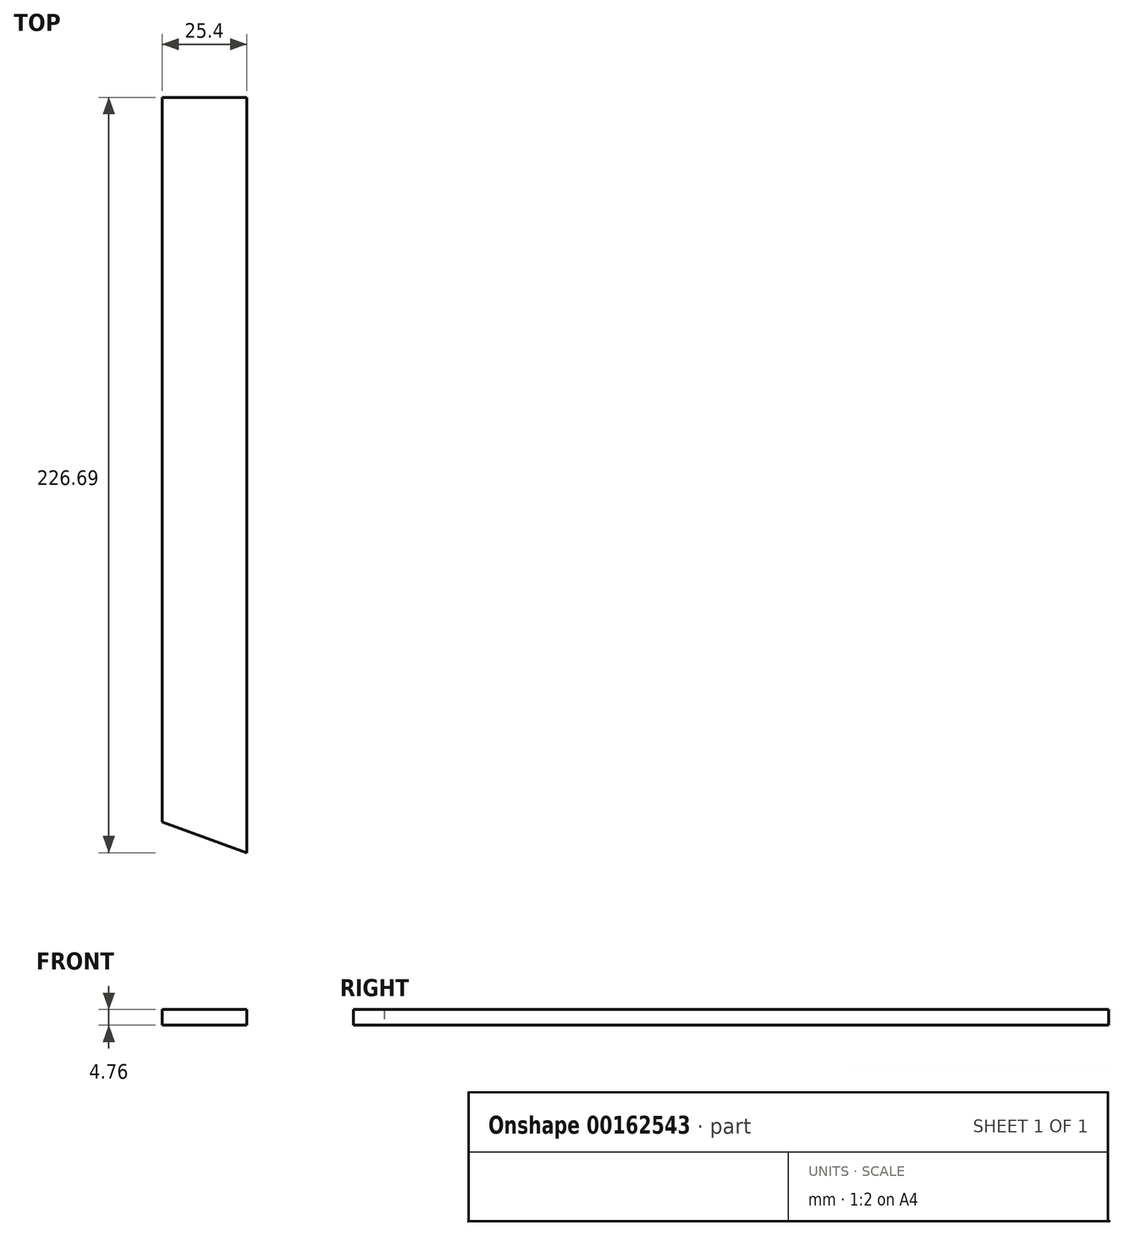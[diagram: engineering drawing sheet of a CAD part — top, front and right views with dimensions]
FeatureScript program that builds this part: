
annotation { "Feature Type Name" : "Feature", "Feature Type Description" : "" }
export const myFeature = defineFeature(function(context is Context, id is Id, definition is map)
    precondition{}
    {
        {
            var Q0;
            Q0=qCreatedBy(makeId("Top.planeOp"),FACE);
            var sketch = newSketch(context, id + "F0", { "sketchPlane" : qUnion([Q0])});
            skLineSegment(sketch, "E0.bottom", {"start": v(12.7, 108.72) * mm, "end": v(-12.7, 108.72) * mm});
            skLineSegment(sketch, "E0.right", {"start": v(-12.7, 108.72) * mm, "end": v(-12.7, -108.72) * mm});
            skPoint(sketch, "E0.middle", {"position": v(0, 0) * mm});
            skPoint(sketch, "E1.end.orphan", {"position": v(12.7, -108.72) * mm});
            skLineSegment(sketch, "E2", {"start": v(12.7, 108.72) * mm, "end": v(12.7, -117.97) * mm});
            skLineSegment(sketch, "E3", {"start": v(-12.7, -108.72) * mm, "end": v(12.7, -117.97) * mm});
            skSolve(sketch);
        }
        {
            var Q0;
            Q0=qSketchRegion(id+"F0",true);
            extrude(context, id + "F1", {"entities" : qUnion([Q0]), "depth" : 4.76 * mm});
        }
    });
